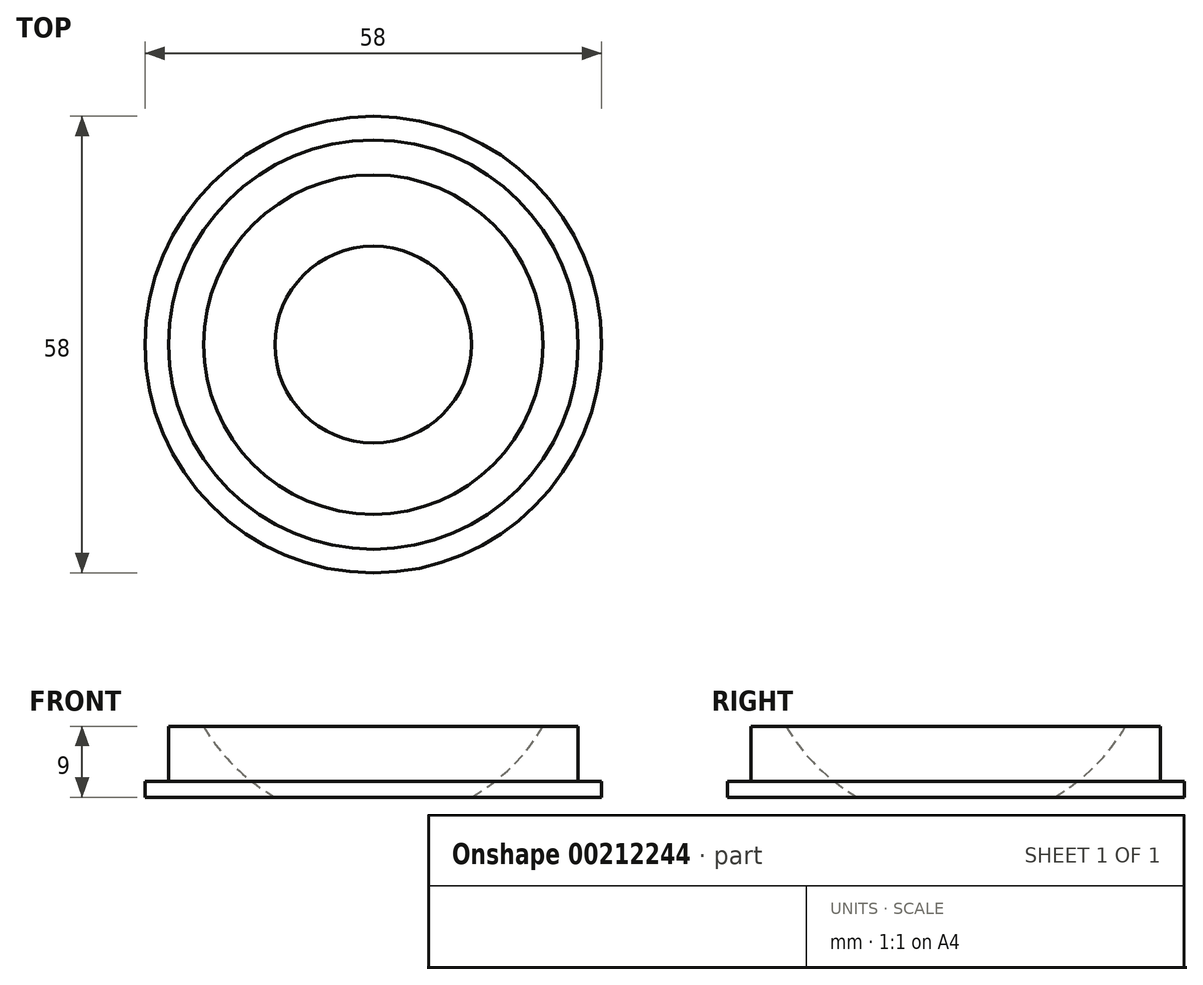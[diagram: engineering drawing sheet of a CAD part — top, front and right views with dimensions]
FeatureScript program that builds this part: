
annotation { "Feature Type Name" : "Feature", "Feature Type Description" : "" }
export const myFeature = defineFeature(function(context is Context, id is Id, definition is map)
    precondition{}
    {
        {
            var Q0;
            Q0=qCreatedBy(makeId("Front.planeOp"),FACE);
            var sketch = newSketch(context, id + "F0", { "sketchPlane" : qUnion([Q0])});
            skLineSegment(sketch, "E0", {"start": v(0, 0) * mm, "end": v(16.5, 0) * mm});
            skLineSegment(sketch, "E1", {"start": v(7.44, 9) * mm, "end": v(3, 9) * mm});
            skLineSegment(sketch, "E2", {"start": v(3, 9) * mm, "end": v(3, 2) * mm});
            skLineSegment(sketch, "E3", {"start": v(3, 2) * mm, "end": v(0, 2) * mm});
            skLineSegment(sketch, "E4", {"start": v(0, 2) * mm, "end": v(0, 0) * mm});
            skArc(sketch, "E5", {"start": v(7.44, 9) * mm, "mid": v(11.38, 3.91) * mm, "end": v(16.5, 0) * mm});
            skLineSegment(sketch, "E6", {"start": v(29, 0) * mm, "end": v(29, 21.65) * mm});
            skSolve(sketch);
        }
        {
            var Q0;
            Q0=makeQuery(id+"F0.imprint","IMPRINT",FACE,{"disambiguationData":[TD([[makeQuery(id+"F0.imprint","IMPRINT",EDGE,{"derivedFrom":sQuery(id+"F0.wireOp",EDGE,"E0")}),1.0]])]});
            var Q1;
            Q1=sQuery(id+"F0.wireOp",EDGE,"E6");
            revolve(context, id + "F1", {"entities" : qUnion([Q0]), "axis" : qUnion([Q1]), "revolveType" : RevolveType.FULL});
        }
    });
